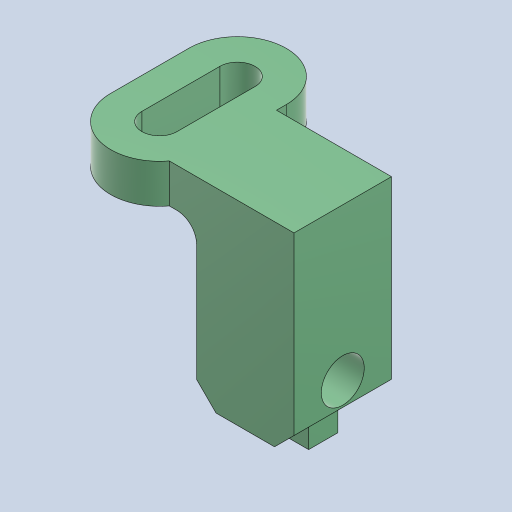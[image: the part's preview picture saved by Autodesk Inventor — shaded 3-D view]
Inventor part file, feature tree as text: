
AUTODESK INVENTOR PART (.ipt)
format: ipt  version: 2023 (Build 270158000, 158)  size: 197,120 bytes
history: native  units: mm
features: sketch x3, extrude x3, other x2, hole x1, fillet x1, chamfer x1
ambient origin geometry x8: Origin, YZ Plane, XZ Plane, XY Plane, X Axis, Y Axis, Z Axis, Center Point
bodies: Body1 (feature_tree)
feature tree (11):
  other  "ソリッド1"
  sketch  "スケッチ1"
  extrude  "押し出し1"  Depth=1.8mm
  extrude  "押し出し4"  Depth=4.0mm
  hole  "穴3"  [1 undecoded]
  fillet  "フィレット3"  Radius=2.0mm
  other  "作業平面2"
  chamfer  "面取り1"  Distance=8.0mm
  extrude  "押し出し5"  Depth=5.0mm
  sketch  "スケッチ6"
  sketch  "スケッチ7"
note: 1 required parameter value undecoded (feature->parameter linkage not recoverable at this tier; creation-order binding heuristic only, values carry confidence <= 0.55)
